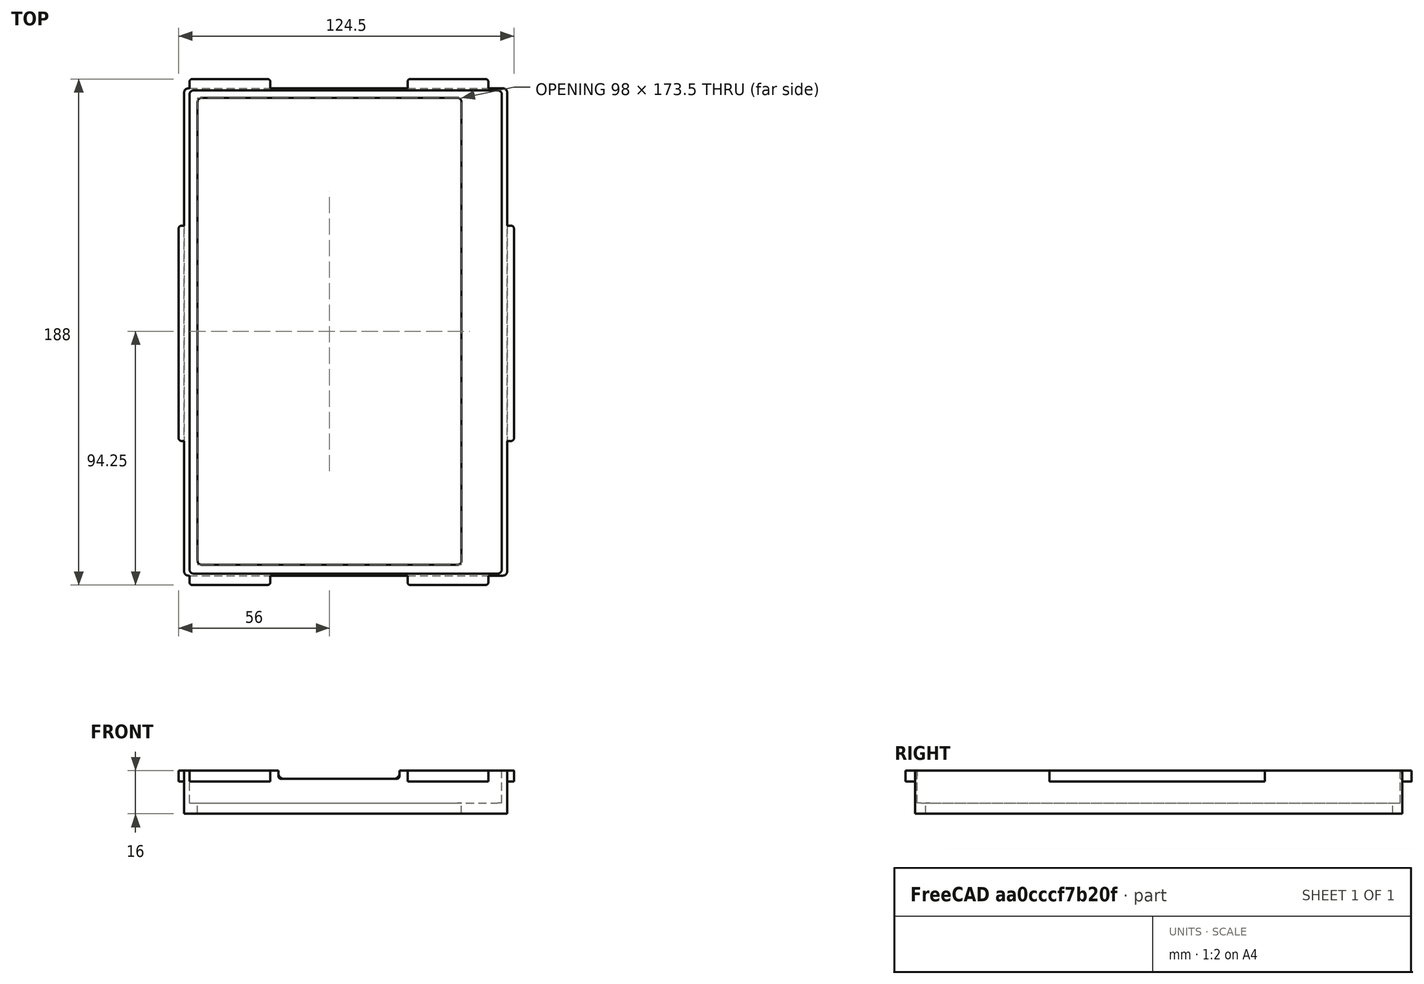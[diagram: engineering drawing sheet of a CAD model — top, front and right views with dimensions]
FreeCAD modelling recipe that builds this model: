
FCSTD DOCUMENT  (FreeCAD 0.20R29177 (Git))
Label: carrier-atoto-s8_test_j
License: All rights reserved
LicenseURL: http://en.wikipedia.org/wiki/All_rights_reserved
objects: Part::Box×12, Part::Fillet×11, Part::MultiFuse×4, Part::Cut×3
note: 30 computed .brp shape members not serialized (recipe doc carries the construction recipe); baked Part::Feature solids carry a one-line shape summary decoded from their .brp

FEATURE [Part::Box] Box  label="Cube"
  AttacherType = Attacher::AttachEngine3D
  Height = 4
  Length = 120
  Placement = pos=(2,0,0) rot=(0,0,1;0rad)
  Width = 181
FEATURE [Part::Box] Box001  label="Cube001"
  AttacherType = Attacher::AttachEngine3D
  Height = 4
  Length = 98
  Placement = pos=(7,4,0) rot=(0,0,1;0rad)
  Width = 173.5
FEATURE [Part::Fillet] Fillet
  Base = -> Box001
  Edges = 4 edges r=1.5: [Edge1,Edge3,Edge5,Edge7]
FEATURE [Part::Fillet] Fillet001
  Base = -> Box
  Edges = 4 edges r=1.5: [Edge1,Edge3,Edge5,Edge7]
FEATURE [Part::Cut] Cut
  Base = -> Fillet001
  Tool = -> Fillet
FEATURE [Part::Box] Box002  label="Cube002"
  AttacherType = Attacher::AttachEngine3D
  Height = 12
  Length = 120
  Placement = pos=(2,0,4) rot=(0,0,1;0rad)
  Width = 181
FEATURE [Part::Box] Box003  label="Cube003"
  AttacherType = Attacher::AttachEngine3D
  Height = 20
  Length = 116
  Placement = pos=(4,0.75,4) rot=(0,0,1;0rad)
  Width = 179.5
FEATURE [Part::Fillet] Fillet002
  Base = -> Box003
  Edges = 4 edges r=1.5: [Edge1,Edge3,Edge5,Edge7]
FEATURE [Part::Fillet] Fillet003
  Base = -> Box002
  Edges = 4 edges r=1.5: [Edge1,Edge3,Edge5,Edge7]
FEATURE [Part::Cut] Cut001
  Base = -> Fillet003
  Tool = -> Fillet002
FEATURE [Part::Box] Box006  label="Cube006"
  AttacherType = Attacher::AttachEngine3D
  Height = 10
  Length = 45
  Placement = pos=(15,-5,0) rot=(0,0,1;0rad)
  Width = 10
FEATURE [Part::Box] Box007  label="Cube007"
  AttacherType = Attacher::AttachEngine3D
  Height = 10
  Length = 45
  Placement = pos=(15,175,0) rot=(0,0,1;0rad)
  Width = 10
FEATURE [Part::MultiFuse] Fusion
  Placement = pos=(22,0,13) rot=(0,0,1;0rad)
  Shapes = -> [Box007,Box006]
FEATURE [Part::Fillet] Fillet004
  Base = -> Fusion
  Edges = 4 edges: [Edge4 r=2,Edge8 r=2,Edge16 r=1,Edge20 r=1]
FEATURE [Part::Cut] Cut002
  Base = -> Cut001
  Tool = -> Fillet004
FEATURE [Part::MultiFuse] Fusion001
  Shapes = -> [Cut,Cut002]
FEATURE [Part::Box] Box008  label="Cube008"
  AttacherType = Attacher::AttachEngine3D
  Height = 4
  Length = 30
  Placement = pos=(85,180.5,5) rot=(0,0,1;0rad)
  Width = 4
FEATURE [Part::Box] Box009  label="Cube009"
  AttacherType = Attacher::AttachEngine3D
  Height = 4
  Length = 30
  Placement = pos=(4,180.5,5) rot=(0,0,1;0rad)
  Width = 4
FEATURE [Part::Box] Box010  label="Cube010"
  AttacherType = Attacher::AttachEngine3D
  Height = 4
  Length = 30
  Placement = pos=(85,-3.5,5) rot=(0,0,1;0rad)
  Width = 4
FEATURE [Part::Box] Box011  label="Cube011"
  AttacherType = Attacher::AttachEngine3D
  Height = 4
  Length = 4
  Placement = pos=(0,50,5) rot=(0,0,1;0rad)
  Width = 80
FEATURE [Part::Box] Box012  label="Cube012"
  AttacherType = Attacher::AttachEngine3D
  Height = 4
  Length = 30
  Placement = pos=(4,-3.5,5) rot=(0,0,1;0rad)
  Width = 4
FEATURE [Part::Box] Box013  label="Cube013"
  AttacherType = Attacher::AttachEngine3D
  Height = 4
  Length = 4
  Placement = pos=(120.5,50,5) rot=(0,0,1;0rad)
  Width = 80
FEATURE [Part::Fillet] Fillet005
  Base = -> Box012
  Edges = 2 edges r=1: [Edge1,Edge5]
FEATURE [Part::Fillet] Fillet006
  Base = -> Box011
  Edges = 2 edges r=1: [Edge1,Edge3]
FEATURE [Part::Fillet] Fillet007
  Base = -> Box010
  Edges = 2 edges r=1: [Edge1,Edge5]
FEATURE [Part::Fillet] Fillet008
  Base = -> Box009
  Edges = 2 edges r=1: [Edge3,Edge7]
FEATURE [Part::Fillet] Fillet009
  Base = -> Box008
  Edges = 2 edges r=1: [Edge3,Edge7]
FEATURE [Part::Fillet] Fillet010
  Base = -> Box013
  Edges = 2 edges r=1: [Edge5,Edge7]
FEATURE [Part::MultiFuse] Fusion002
  Placement = pos=(0,0,7) rot=(0,0,1;0rad)
  Shapes = -> [Fillet005,Fillet006,Fillet007,Fillet008,Fillet009,Fillet010]
FEATURE [Part::MultiFuse] Fusion003
  Shapes = -> [Fusion001,Fusion002]
